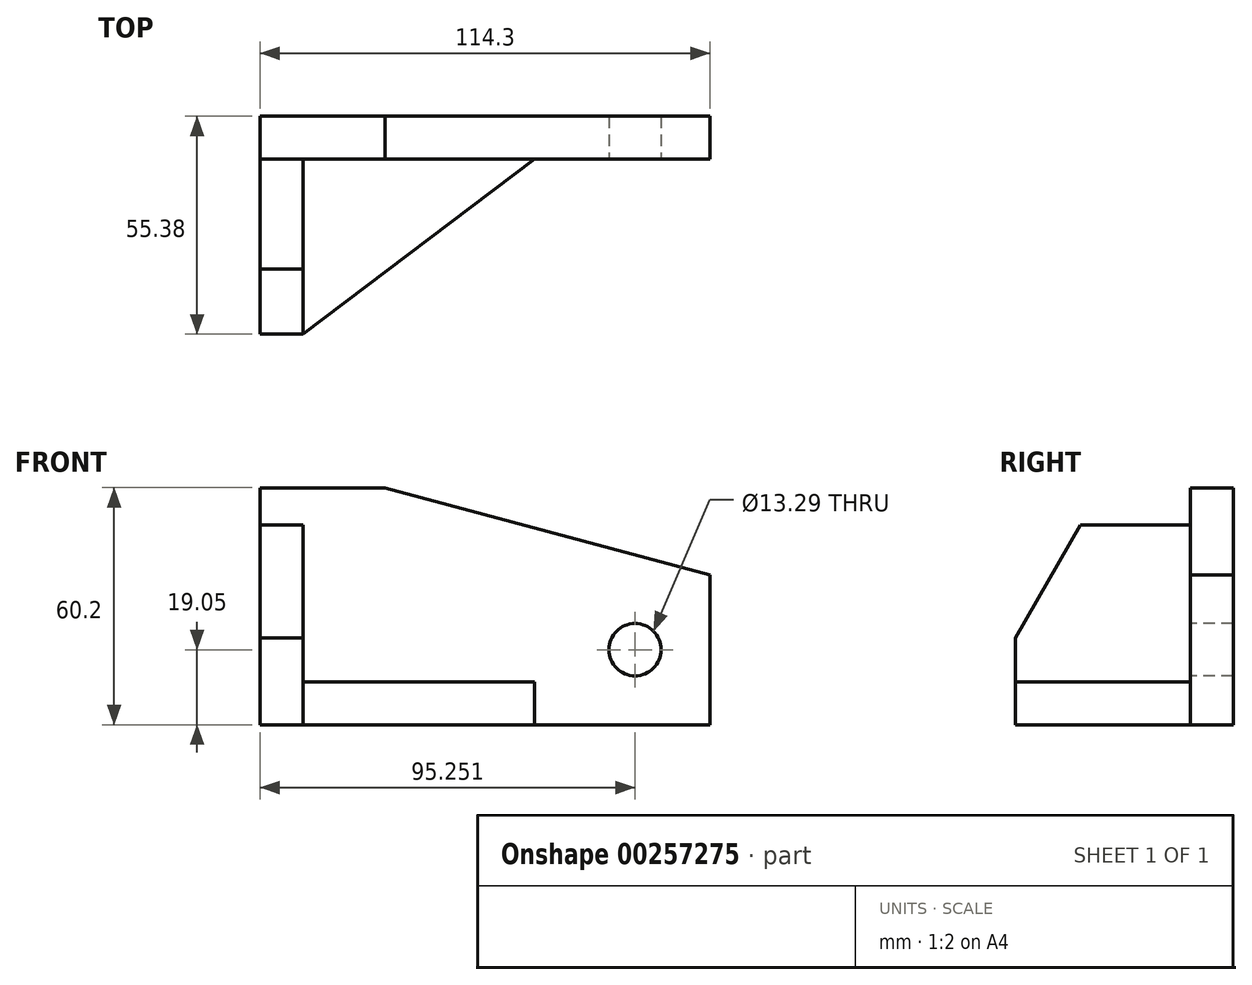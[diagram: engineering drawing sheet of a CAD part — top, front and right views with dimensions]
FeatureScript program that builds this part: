
annotation { "Feature Type Name" : "Feature", "Feature Type Description" : "" }
export const myFeature = defineFeature(function(context is Context, id is Id, definition is map)
    precondition{}
    {
        {
            var Q0;
            Q0=qCreatedBy(makeId("Top.planeOp"),FACE);
            var sketch = newSketch(context, id + "F0", { "sketchPlane" : qUnion([Q0])});
            skLineSegment(sketch, "E0", {"start": v(-40.34, 19.95) * mm, "end": v(-8.59, 19.95) * mm});
            skLineSegment(sketch, "E1", {"start": v(-40.34, 9.02) * mm, "end": v(-8.59, 9.02) * mm});
            skLineSegment(sketch, "E2", {"start": v(-40.34, 19.95) * mm, "end": v(-40.34, 9.02) * mm});
            skLineSegment(sketch, "E3", {"start": v(-8.59, 19.95) * mm, "end": v(-8.59, 9.02) * mm});
            skLineSegment(sketch, "E4", {"start": v(-8.59, 19.95) * mm, "end": v(73.96, 19.95) * mm});
            skLineSegment(sketch, "E5", {"start": v(-8.59, 9.02) * mm, "end": v(73.96, 9.02) * mm});
            skLineSegment(sketch, "E6", {"start": v(73.96, 9.02) * mm, "end": v(73.96, 19.95) * mm});
            skLineSegment(sketch, "E7", {"start": v(-40.34, 9.02) * mm, "end": v(-40.34, -7.71) * mm});
            skLineSegment(sketch, "E8", {"start": v(-40.34, -7.71) * mm, "end": v(-29.42, -7.71) * mm});
            skLineSegment(sketch, "E9", {"start": v(-29.42, -7.71) * mm, "end": v(-29.42, 9.02) * mm});
            skLineSegment(sketch, "E10", {"start": v(-40.34, -7.71) * mm, "end": v(-40.34, -35.43) * mm});
            skLineSegment(sketch, "E11", {"start": v(-29.42, -7.71) * mm, "end": v(-29.42, -35.43) * mm});
            skLineSegment(sketch, "E12", {"start": v(-40.34, -35.43) * mm, "end": v(-29.42, -35.43) * mm});
            skLineSegment(sketch, "E13", {"start": v(-29.42, -35.43) * mm, "end": v(29.34, 9.02) * mm});
            skSolve(sketch);
        }
        {
            var Q0;
            Q0=makeQuery(id+"F0.imprint","IMPRINT",FACE,{"disambiguationData":[TD([[makeQuery(id+"F0.imprint","IMPRINT",EDGE,{"derivedFrom":sQuery(id+"F0.wireOp",EDGE,"E0")}),-1.0]])]});
            var Q1;
            Q1=makeQuery(id+"F0.imprint","IMPRINT",FACE,{"disambiguationData":[TD([[makeQuery(id+"F0.imprint","IMPRINT",EDGE,{"derivedFrom":sQuery(id+"F0.wireOp",EDGE,"E3")}),1.0]])]});
            extrude(context, id + "F1", {"entities" : qUnion([Q0, Q1]), "depth" : 60.2 * mm});
        }
        {
            var Q0;
            {var subQ0=sQuery(id+"F0.wireOp",EDGE,"E7");Q0=makeQuery(id+"F0.imprint","IMPRINT",FACE,{"disambiguationData":[TD([[makeQuery(id+"F0.imprint","IMPRINT",EDGE,{"derivedFrom":subQ0}),1.0]])]});}
            var Q1;
            Q1=makeQuery(id+"F0.imprint","IMPRINT",FACE,{"disambiguationData":[TD([[makeQuery(id+"F0.imprint","IMPRINT",EDGE,{"derivedFrom":sQuery(id+"F0.wireOp",EDGE,"E8")}),-1.0]])]});
            extrude(context, id + "F2", {"entities" : qUnion([Q0, Q1]), "operationType" : NewBodyOperationType.ADD, "depth" : 50.8 * mm});
        }
        {
            var Q0;
            {var subQ4=sQuery(id+"F0.wireOp",EDGE,"E9");Q0=makeQuery(id+"F0.imprint","IMPRINT",FACE,{"disambiguationData":[TD([[makeQuery(id+"F0.imprint","IMPRINT",EDGE,{"derivedFrom":subQ4}),-1.0]])]});}
            extrude(context, id + "F3", {"entities" : qUnion([Q0]), "operationType" : NewBodyOperationType.ADD, "depth" : 10.92 * mm});
        }
        {
            var Q0;
            Q0=makeQuery(id+"F1.opExtrude","SWEPT_FACE",FACE,{"disambiguationData":[OSD([sQuery(id+"F0.wireOp",EDGE,"E1"),sQuery(id+"F0.wireOp",EDGE,"E5")])]});
            var sketch = newSketch(context, id + "F4", { "sketchPlane" : qUnion([Q0])});
            skCircle(sketch, "E14", {"center": v(54.91, 19.05) * mm, "radius": 6.64 * mm});
            skSolve(sketch);
        }
        {
            var Q0;
            Q0=makeQuery(id+"F4.imprint","IMPRINT",FACE,{"disambiguationData":[TD([[makeQuery(id+"F4.imprint","IMPRINT",EDGE,{"derivedFrom":sQuery(id+"F4.wireOp",EDGE,"E14")}),1.0]])]});
            extrude(context, id + "F5", {"entities" : qUnion([Q0]), "operationType" : NewBodyOperationType.REMOVE, "endBound" : BoundingType.THROUGH_ALL, "oppositeDirection" : true, "depth" : 25.4 * mm});
        }
        {
            var Q0;
            Q0=makeQuery(id+"F2.opExtrude","CAP_EDGE",EDGE,{"disambiguationData":[OSD([sQuery(id+"F0.wireOp",EDGE,"E12")])],"isStart":false});
            chamfer(context, id + "F6", {"entities" : qUnion([Q0]), "chamferType" : ChamferType.OFFSET_ANGLE, "width" : 28.7 * mm, "oppositeDirection" : true, "angle" : 30 * degree, "tangentPropagation" : true});
        }
        {
            var Q0;
            Q0=makeQuery(id+"F1.opExtrude","CAP_EDGE",EDGE,{"disambiguationData":[OSD([sQuery(id+"F0.wireOp",EDGE,"E6")])],"isStart":false});
            chamfer(context, id + "F7", {"entities" : qUnion([Q0]), "chamferType" : ChamferType.OFFSET_ANGLE, "width" : 82.55 * mm, "oppositeDirection" : false, "angle" : 15 * degree, "tangentPropagation" : true});
        }
    });
